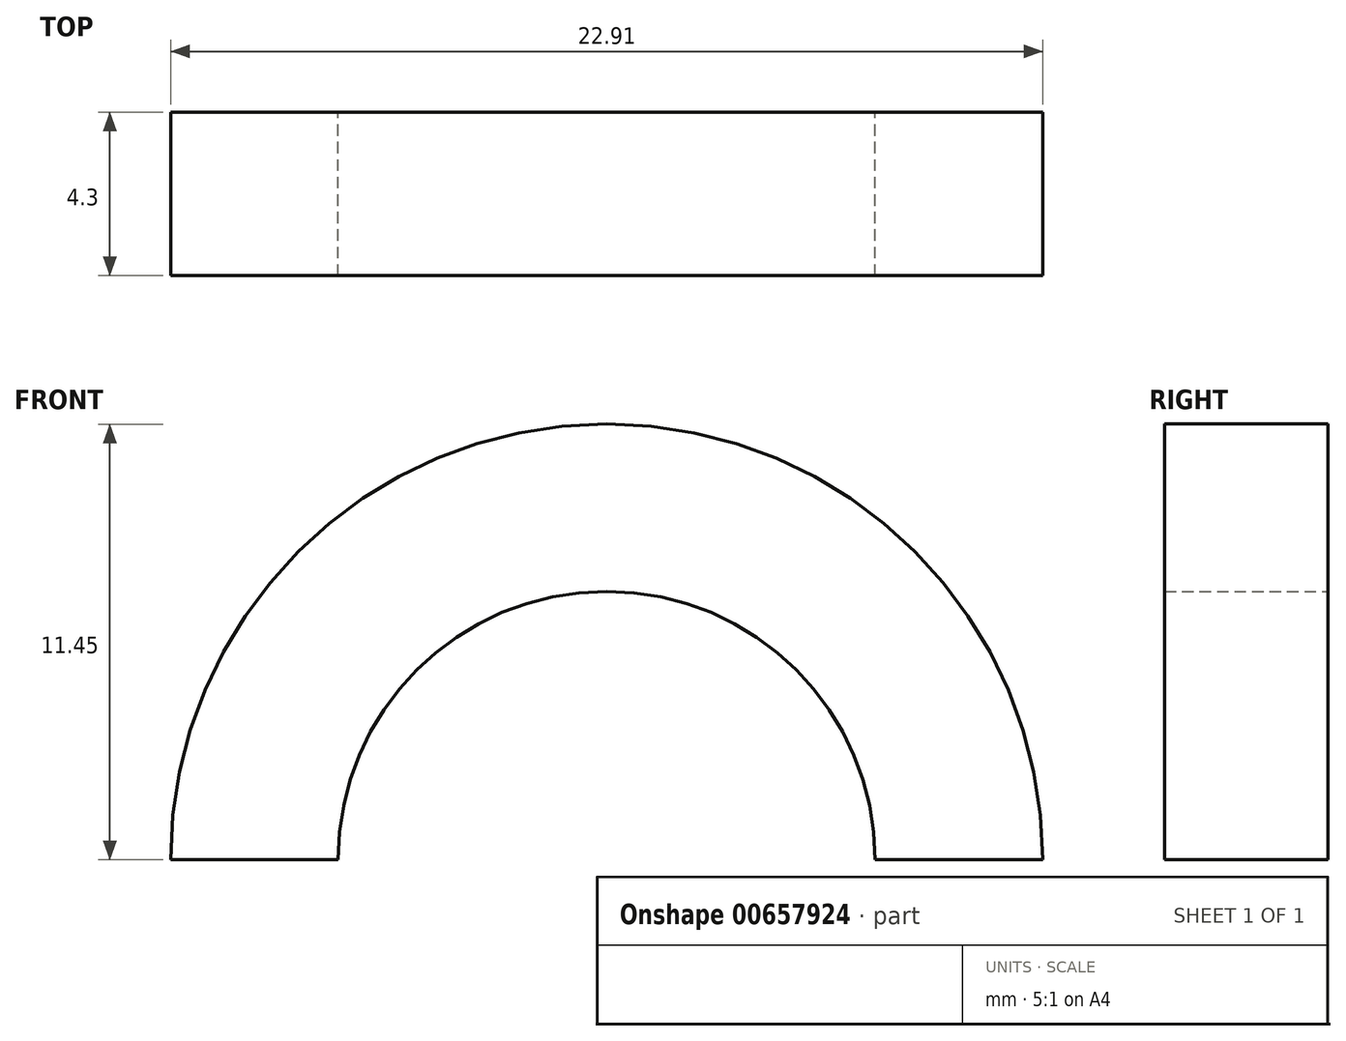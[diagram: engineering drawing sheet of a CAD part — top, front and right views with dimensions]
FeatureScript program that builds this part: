
annotation { "Feature Type Name" : "Feature", "Feature Type Description" : "" }
export const myFeature = defineFeature(function(context is Context, id is Id, definition is map)
    precondition{}
    {
        {
            var Q0;
            Q0=qCreatedBy(makeId("Front.planeOp"),FACE);
            var sketch = newSketch(context, id + "F0", { "sketchPlane" : qUnion([Q0])});
            skArc(sketch, "E0", {"start": v(-21.27, 17.08) * mm, "mid": v(-32.73, 28.53) * mm, "end": v(-44.18, 17.08) * mm});
            skArc(sketch, "E1.0", {"start": v(-25.67, 17.08) * mm, "mid": v(-32.73, 24.13) * mm, "end": v(-39.78, 17.08) * mm});
            skLineSegment(sketch, "E2", {"start": v(-44.18, 17.08) * mm, "end": v(-39.78, 17.08) * mm});
            skLineSegment(sketch, "E3", {"start": v(-25.67, 17.08) * mm, "end": v(-21.27, 17.08) * mm});
            skSolve(sketch);
        }
        {
            var Q0;
            Q0 = qSketchRegion(id + "F0", true);
            extrude(context, id + "F1", {"entities" : qUnion([Q0]), "depth" : 4.3 * mm, "offsetDistance" : 25 * mm});
        }
    });
